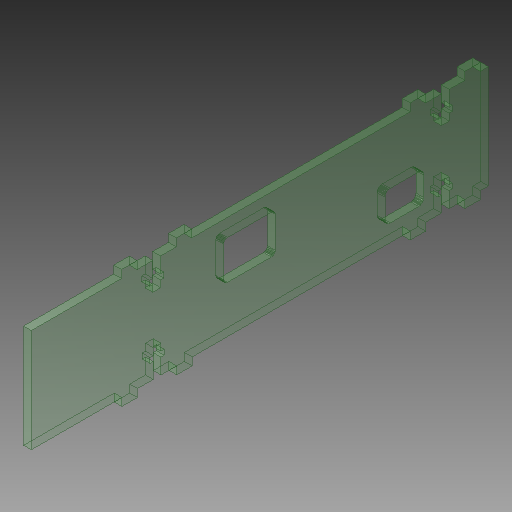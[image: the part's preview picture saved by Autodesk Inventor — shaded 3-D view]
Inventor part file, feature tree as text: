
AUTODESK INVENTOR PART (.ipt)
format: ipt  version: 2017 (Build 210142000, 142)  size: 296,448 bytes
history: native  units: mm
features: extrude x1, sketch x1
ambient origin geometry x8: Origin, YZ Plane, XZ Plane, XY Plane, X Axis, Y Axis, Z Axis, Center Point
bodies: Solid1 (feature_tree)
feature tree (2):
  extrude  "Extrusion1"  [1 undecoded]
  sketch  "Sketch1"  dims[d0=3.0mm d1=0.0mm]
note: 1 required parameter value undecoded (feature->parameter linkage not recoverable at this tier; creation-order binding heuristic only, values carry confidence <= 0.55)
